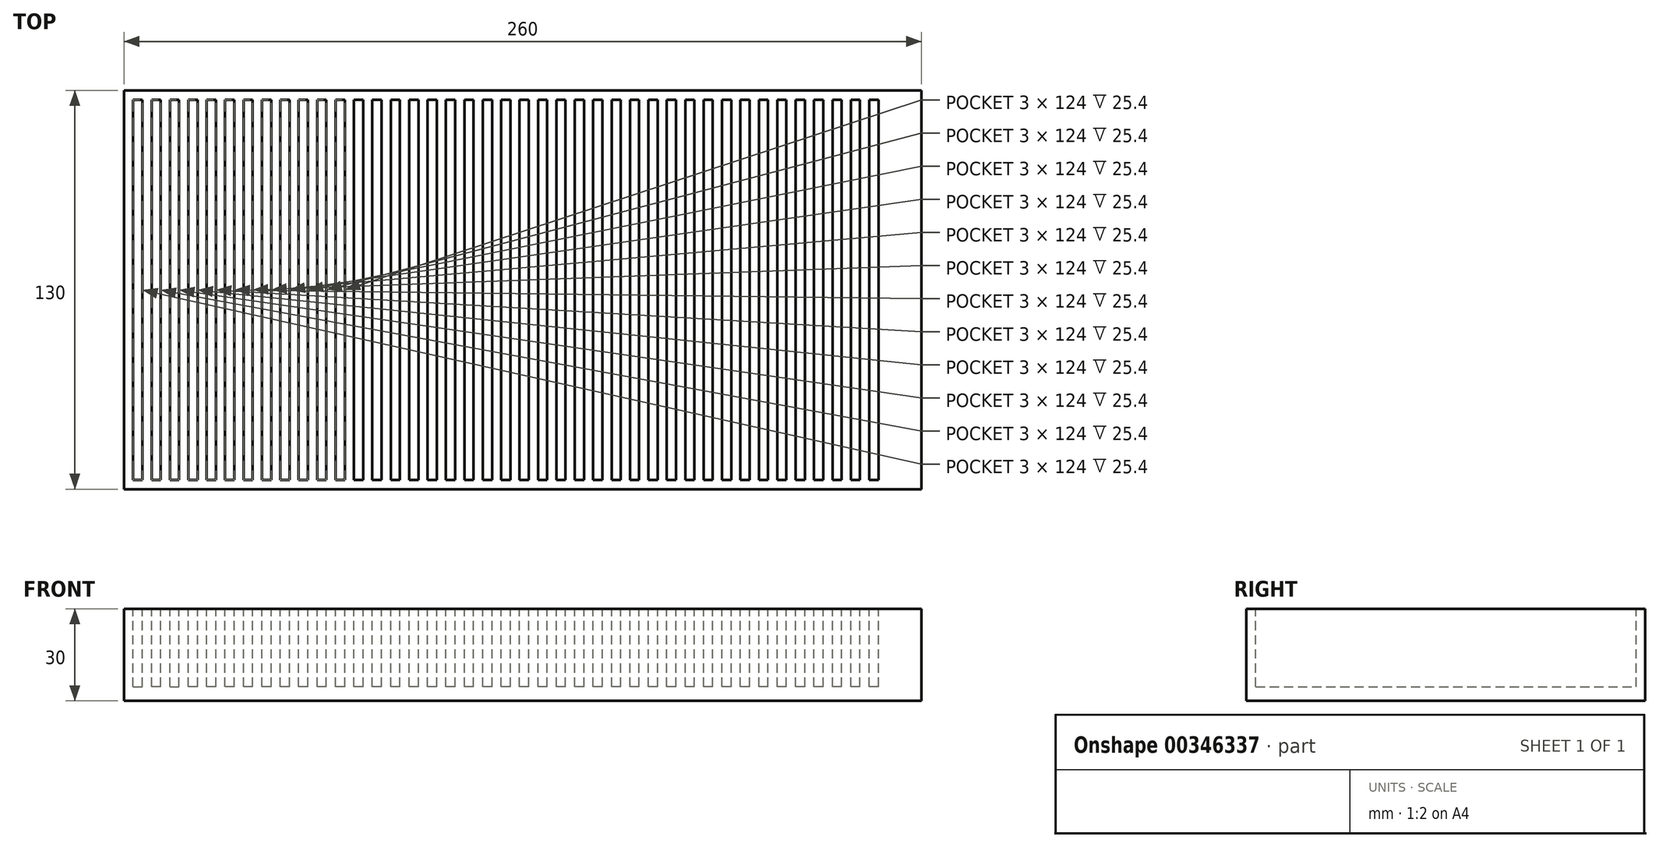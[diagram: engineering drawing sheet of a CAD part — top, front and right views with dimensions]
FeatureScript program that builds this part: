
annotation { "Feature Type Name" : "Feature", "Feature Type Description" : "" }
export const myFeature = defineFeature(function(context is Context, id is Id, definition is map)
    precondition{}
    {
        {
            var Q0;
            Q0=qCreatedBy(makeId("Top.planeOp"),FACE);
            var sketch = newSketch(context, id + "F0", { "sketchPlane" : qUnion([Q0])});
            skLineSegment(sketch, "E0.bottom", {"start": v(-130, 65) * mm, "end": v(130, 65) * mm});
            skLineSegment(sketch, "E0.top", {"start": v(-130, -65) * mm, "end": v(130, -65) * mm});
            skLineSegment(sketch, "E0.left", {"start": v(-130, 65) * mm, "end": v(-130, -65) * mm});
            skLineSegment(sketch, "E0.right", {"start": v(130, 65) * mm, "end": v(130, -65) * mm});
            skPoint(sketch, "E0.middle", {"position": v(0, 0) * mm});
            skSolve(sketch);
        }
        {
            var Q0;
            Q0=makeQuery(id+"F0.imprint","IMPRINT",FACE,{"disambiguationData":[TD([[makeQuery(id+"F0.imprint","IMPRINT",EDGE,{"derivedFrom":sQuery(id+"F0.wireOp",EDGE,"E0.bottom")}),-1.0]])]});
            extrude(context, id + "F1", {"entities" : qUnion([Q0]), "depth" : 30 * mm});
        }
        {
            var Q0;
            Q0=makeQuery(id+"F1.opExtrude","CAP_FACE",FACE,{"disambiguationData":[OSD([sQuery(id+"F0.wireOp",EDGE,"E0.bottom"),sQuery(id+"F0.wireOp",EDGE,"E0.top"),sQuery(id+"F0.wireOp",EDGE,"E0.left"),sQuery(id+"F0.wireOp",EDGE,"E0.right")])],"isStart":false});
            var sketch = newSketch(context, id + "F2", { "sketchPlane" : qUnion([Q0])});
            skLineSegment(sketch, "E1.0", {"start": v(-127, 62) * mm, "end": v(-127, -62) * mm});
            skLineSegment(sketch, "E1.1", {"start": v(127, 62) * mm, "end": v(-127, 62) * mm});
            skLineSegment(sketch, "E1.2", {"start": v(127, -62) * mm, "end": v(127, 62) * mm});
            skLineSegment(sketch, "E1.3", {"start": v(-127, -62) * mm, "end": v(127, -62) * mm});
            skLineSegment(sketch, "E2", {"start": v(-127, 0) * mm, "end": v(-124, 0) * mm});
            skLineSegment(sketch, "E3", {"start": v(-124, 0) * mm, "end": v(-121, 0) * mm});
            skLineSegment(sketch, "E4", {"start": v(-121, 0) * mm, "end": v(-118, 0) * mm});
            skLineSegment(sketch, "E5", {"start": v(-118, 0) * mm, "end": v(-115, 0) * mm});
            skLineSegment(sketch, "E6", {"start": v(-115, 0) * mm, "end": v(-112, 0) * mm});
            skLineSegment(sketch, "E7", {"start": v(-112, 0) * mm, "end": v(-109, 0) * mm});
            skLineSegment(sketch, "E8", {"start": v(-109, 0) * mm, "end": v(-106, 0) * mm});
            skLineSegment(sketch, "E9", {"start": v(-106, 0) * mm, "end": v(-103, 0) * mm});
            skLineSegment(sketch, "E10", {"start": v(-103, 0) * mm, "end": v(-100, 0) * mm});
            skLineSegment(sketch, "E11", {"start": v(-100, 0) * mm, "end": v(-97, 0) * mm});
            skLineSegment(sketch, "E12", {"start": v(-97, 0) * mm, "end": v(-94, 0) * mm});
            skLineSegment(sketch, "E13", {"start": v(-94, 0) * mm, "end": v(-91, 0) * mm});
            skLineSegment(sketch, "E14", {"start": v(-91, 0) * mm, "end": v(-88, 0) * mm});
            skLineSegment(sketch, "E15", {"start": v(-88, 0) * mm, "end": v(-85, 0) * mm});
            skLineSegment(sketch, "E16", {"start": v(-85, 0) * mm, "end": v(-82, 0) * mm});
            skLineSegment(sketch, "E17", {"start": v(-82, 0) * mm, "end": v(-79, 0) * mm});
            skLineSegment(sketch, "E18", {"start": v(-79, 0) * mm, "end": v(-76, 0) * mm});
            skLineSegment(sketch, "E19", {"start": v(-124, 0) * mm, "end": v(-124, 62) * mm});
            skLineSegment(sketch, "E20", {"start": v(-121, 0) * mm, "end": v(-121, 4.03) * mm});
            skLineSegment(sketch, "E21", {"start": v(-121, 62) * mm, "end": v(-121, 0) * mm});
            skLineSegment(sketch, "E22", {"start": v(-118, 0) * mm, "end": v(-118, 62) * mm});
            skLineSegment(sketch, "E23", {"start": v(-118, 62) * mm, "end": v(-115, 62) * mm});
            skLineSegment(sketch, "E24", {"start": v(-115, 62) * mm, "end": v(-115, 0) * mm});
            skLineSegment(sketch, "E25", {"start": v(-112, 0) * mm, "end": v(-112, 62) * mm});
            skLineSegment(sketch, "E26", {"start": v(-112, 62) * mm, "end": v(-109, 62) * mm});
            skLineSegment(sketch, "E27", {"start": v(-109, 62) * mm, "end": v(-109, 0) * mm});
            skLineSegment(sketch, "E28", {"start": v(-106, 0) * mm, "end": v(-106, 62) * mm});
            skLineSegment(sketch, "E29", {"start": v(-106, 62) * mm, "end": v(-103, 62) * mm});
            skLineSegment(sketch, "E30", {"start": v(-103, 62) * mm, "end": v(-103, -62) * mm});
            skLineSegment(sketch, "E31", {"start": v(-103, -62) * mm, "end": v(-100, -62) * mm});
            skLineSegment(sketch, "E32", {"start": v(-100, -62) * mm, "end": v(-100, 62) * mm});
            skLineSegment(sketch, "E33", {"start": v(-100, 62) * mm, "end": v(-97, 62) * mm});
            skLineSegment(sketch, "E34", {"start": v(-97, 62) * mm, "end": v(-97, -62) * mm});
            skLineSegment(sketch, "E35", {"start": v(-97, -62) * mm, "end": v(-94, -62) * mm});
            skLineSegment(sketch, "E36", {"start": v(-94, -62) * mm, "end": v(-94, 62) * mm});
            skLineSegment(sketch, "E37", {"start": v(-94, 62) * mm, "end": v(-91, 62) * mm});
            skLineSegment(sketch, "E38", {"start": v(-91, 62) * mm, "end": v(-91, -62) * mm});
            skLineSegment(sketch, "E39", {"start": v(-91, -62) * mm, "end": v(-88, -62) * mm});
            skLineSegment(sketch, "E40", {"start": v(-88, -62) * mm, "end": v(-88, 62) * mm});
            skLineSegment(sketch, "E41", {"start": v(-88, 62) * mm, "end": v(-85, 62) * mm});
            skLineSegment(sketch, "E42", {"start": v(-85, 62) * mm, "end": v(-85, -62) * mm});
            skLineSegment(sketch, "E43", {"start": v(-85, -62) * mm, "end": v(-82, -62) * mm});
            skLineSegment(sketch, "E44", {"start": v(-82, -62) * mm, "end": v(-82, 62) * mm});
            skLineSegment(sketch, "E45", {"start": v(-82, 62) * mm, "end": v(-79, 62) * mm});
            skLineSegment(sketch, "E46", {"start": v(-79, 62) * mm, "end": v(-79, -62) * mm});
            skLineSegment(sketch, "E47", {"start": v(-79, -62) * mm, "end": v(-76, -62) * mm});
            skLineSegment(sketch, "E48", {"start": v(-76, -62) * mm, "end": v(-76, 62) * mm});
            skLineSegment(sketch, "E49", {"start": v(-106, 0) * mm, "end": v(-106, -62) * mm});
            skLineSegment(sketch, "E50", {"start": v(-106, -62) * mm, "end": v(-109, -62) * mm});
            skLineSegment(sketch, "E51", {"start": v(-109, -62) * mm, "end": v(-109, 0) * mm});
            skLineSegment(sketch, "E52", {"start": v(-112, 0) * mm, "end": v(-112, -62) * mm});
            skLineSegment(sketch, "E53", {"start": v(-112, -62) * mm, "end": v(-115, -62) * mm});
            skLineSegment(sketch, "E54", {"start": v(-115, -62) * mm, "end": v(-115, 0) * mm});
            skLineSegment(sketch, "E55", {"start": v(-118, 0) * mm, "end": v(-118, -62) * mm});
            skLineSegment(sketch, "E56", {"start": v(-118, -62) * mm, "end": v(-121, -62) * mm});
            skLineSegment(sketch, "E57", {"start": v(-121, -62) * mm, "end": v(-121, 0) * mm});
            skLineSegment(sketch, "E58", {"start": v(-124, 0) * mm, "end": v(-124, -62) * mm});
            skLineSegment(sketch, "E59", {"start": v(-76, 62) * mm, "end": v(-73, 62) * mm});
            skLineSegment(sketch, "E60", {"start": v(-73, 62) * mm, "end": v(-73, -62) * mm});
            skLineSegment(sketch, "E61", {"start": v(-73, -62) * mm, "end": v(-70, -62) * mm});
            skLineSegment(sketch, "E62", {"start": v(-70, -62) * mm, "end": v(-70, 62) * mm});
            skLineSegment(sketch, "E63", {"start": v(-70, 62) * mm, "end": v(-67, 62) * mm});
            skLineSegment(sketch, "E64", {"start": v(-67, 62) * mm, "end": v(-67, -62) * mm});
            skLineSegment(sketch, "E65", {"start": v(-67, -62) * mm, "end": v(-64, -62) * mm});
            skLineSegment(sketch, "E66", {"start": v(-64, -62) * mm, "end": v(-64, 62) * mm});
            skLineSegment(sketch, "E67", {"start": v(-64, 62) * mm, "end": v(-61, 62) * mm});
            skLineSegment(sketch, "E68", {"start": v(-61, 62) * mm, "end": v(-61, -62) * mm});
            skLineSegment(sketch, "E69", {"start": v(-61, -62) * mm, "end": v(-58, -62) * mm});
            skLineSegment(sketch, "E70", {"start": v(-58, -62) * mm, "end": v(-58, 62) * mm});
            skLineSegment(sketch, "E71", {"start": v(-58, 62) * mm, "end": v(-55, 62) * mm});
            skLineSegment(sketch, "E72", {"start": v(-55, 62) * mm, "end": v(-55, -62) * mm});
            skLineSegment(sketch, "E73", {"start": v(-55, -62) * mm, "end": v(-52, -62) * mm});
            skLineSegment(sketch, "E74", {"start": v(-52, -62) * mm, "end": v(-52, 62) * mm});
            skLineSegment(sketch, "E75", {"start": v(-52, 62) * mm, "end": v(-49, 62) * mm});
            skLineSegment(sketch, "E76", {"start": v(-49, 62) * mm, "end": v(-49, -62) * mm});
            skLineSegment(sketch, "E77", {"start": v(-49, -62) * mm, "end": v(-46, -62) * mm});
            skLineSegment(sketch, "E78", {"start": v(-46, -62) * mm, "end": v(-46, 62) * mm});
            skLineSegment(sketch, "E79", {"start": v(-46, 62) * mm, "end": v(-43, 62) * mm});
            skLineSegment(sketch, "E80", {"start": v(-43, 62) * mm, "end": v(-43, -62) * mm});
            skLineSegment(sketch, "E81", {"start": v(-43, -62) * mm, "end": v(-40, -62) * mm});
            skLineSegment(sketch, "E82", {"start": v(-40, -62) * mm, "end": v(-40, 62) * mm});
            skLineSegment(sketch, "E83", {"start": v(-40, 62) * mm, "end": v(-37, 62) * mm});
            skLineSegment(sketch, "E84", {"start": v(-37, 62) * mm, "end": v(-37, -62) * mm});
            skLineSegment(sketch, "E85", {"start": v(-37, -62) * mm, "end": v(-34, -62) * mm});
            skLineSegment(sketch, "E86", {"start": v(-34, -62) * mm, "end": v(-34, 62) * mm});
            skLineSegment(sketch, "E87", {"start": v(-34, 62) * mm, "end": v(-31, 62) * mm});
            skLineSegment(sketch, "E88", {"start": v(-31, 62) * mm, "end": v(-31, -62) * mm});
            skLineSegment(sketch, "E89", {"start": v(-31, -62) * mm, "end": v(-28, -62) * mm});
            skLineSegment(sketch, "E90", {"start": v(-28, -62) * mm, "end": v(-28, 62) * mm});
            skLineSegment(sketch, "E91", {"start": v(-28, 62) * mm, "end": v(-25, 62) * mm});
            skLineSegment(sketch, "E92", {"start": v(-25, 62) * mm, "end": v(-25, -62) * mm});
            skLineSegment(sketch, "E93", {"start": v(-25, -62) * mm, "end": v(-22, -62) * mm});
            skLineSegment(sketch, "E94", {"start": v(-22, -62) * mm, "end": v(-22, 62) * mm});
            skLineSegment(sketch, "E95", {"start": v(-22, 62) * mm, "end": v(-19, 62) * mm});
            skLineSegment(sketch, "E96", {"start": v(-19, 62) * mm, "end": v(-19, -62) * mm});
            skLineSegment(sketch, "E97", {"start": v(-19, -62) * mm, "end": v(-16, -62) * mm});
            skLineSegment(sketch, "E98", {"start": v(-16, -62) * mm, "end": v(-16, 62) * mm});
            skLineSegment(sketch, "E99", {"start": v(-16, 62) * mm, "end": v(-13, 62) * mm});
            skLineSegment(sketch, "E100", {"start": v(-13, 62) * mm, "end": v(-13, -62) * mm});
            skLineSegment(sketch, "E101", {"start": v(-13, -62) * mm, "end": v(-10, -62) * mm});
            skLineSegment(sketch, "E102", {"start": v(-10, -62) * mm, "end": v(-10, 62) * mm});
            skLineSegment(sketch, "E103", {"start": v(-10, 62) * mm, "end": v(-7, 62) * mm});
            skLineSegment(sketch, "E104", {"start": v(-7, 62) * mm, "end": v(-7, -62) * mm});
            skLineSegment(sketch, "E105", {"start": v(-7, -62) * mm, "end": v(-4, -62) * mm});
            skLineSegment(sketch, "E106", {"start": v(-4, -62) * mm, "end": v(-4, 62) * mm});
            skLineSegment(sketch, "E107", {"start": v(-4, 62) * mm, "end": v(-1, 62) * mm});
            skLineSegment(sketch, "E108", {"start": v(-1, 62) * mm, "end": v(-1, -62) * mm});
            skLineSegment(sketch, "E109", {"start": v(-1, -62) * mm, "end": v(2, -62) * mm});
            skLineSegment(sketch, "E110", {"start": v(2, -62) * mm, "end": v(2, 62) * mm});
            skLineSegment(sketch, "E111", {"start": v(2, 62) * mm, "end": v(5, 62) * mm});
            skLineSegment(sketch, "E112", {"start": v(5, 62) * mm, "end": v(5, -62) * mm});
            skLineSegment(sketch, "E113", {"start": v(5, -62) * mm, "end": v(8, -62) * mm});
            skLineSegment(sketch, "E114", {"start": v(8, -62) * mm, "end": v(8, 62) * mm});
            skLineSegment(sketch, "E115", {"start": v(8, 62) * mm, "end": v(11, 62) * mm});
            skLineSegment(sketch, "E116", {"start": v(11, 62) * mm, "end": v(11, -62) * mm});
            skLineSegment(sketch, "E117", {"start": v(11, -62) * mm, "end": v(14, -62) * mm});
            skLineSegment(sketch, "E118", {"start": v(14, -62) * mm, "end": v(14, 62) * mm});
            skLineSegment(sketch, "E119", {"start": v(14, 62) * mm, "end": v(17, 62) * mm});
            skLineSegment(sketch, "E120", {"start": v(17, 62) * mm, "end": v(17, -62) * mm});
            skLineSegment(sketch, "E121", {"start": v(17, -62) * mm, "end": v(20, -62) * mm});
            skLineSegment(sketch, "E122", {"start": v(20, -62) * mm, "end": v(20, 62) * mm});
            skLineSegment(sketch, "E123", {"start": v(20, 62) * mm, "end": v(23, 62) * mm});
            skLineSegment(sketch, "E124", {"start": v(23, 62) * mm, "end": v(23, -62) * mm});
            skLineSegment(sketch, "E125", {"start": v(23, -62) * mm, "end": v(26, -62) * mm});
            skLineSegment(sketch, "E126", {"start": v(26, -62) * mm, "end": v(26, 62) * mm});
            skLineSegment(sketch, "E127", {"start": v(26, 62) * mm, "end": v(29, 62) * mm});
            skLineSegment(sketch, "E128", {"start": v(29, 62) * mm, "end": v(29, -62) * mm});
            skLineSegment(sketch, "E129", {"start": v(29, -62) * mm, "end": v(32, -62) * mm});
            skLineSegment(sketch, "E130", {"start": v(32, -62) * mm, "end": v(32, 62) * mm});
            skLineSegment(sketch, "E131", {"start": v(32, 62) * mm, "end": v(35, 62) * mm});
            skLineSegment(sketch, "E132", {"start": v(35, 62) * mm, "end": v(35, -62) * mm});
            skLineSegment(sketch, "E133", {"start": v(35, -62) * mm, "end": v(38, -62) * mm});
            skLineSegment(sketch, "E134", {"start": v(38, -62) * mm, "end": v(38, 62) * mm});
            skLineSegment(sketch, "E135", {"start": v(38, 62) * mm, "end": v(41, 62) * mm});
            skLineSegment(sketch, "E136", {"start": v(41, 62) * mm, "end": v(41, -62) * mm});
            skLineSegment(sketch, "E137", {"start": v(41, -62) * mm, "end": v(44, -62) * mm});
            skLineSegment(sketch, "E138", {"start": v(44, -62) * mm, "end": v(44, 62) * mm});
            skLineSegment(sketch, "E139", {"start": v(44, 62) * mm, "end": v(47, 62) * mm});
            skLineSegment(sketch, "E140", {"start": v(47, 62) * mm, "end": v(47, -62) * mm});
            skLineSegment(sketch, "E141", {"start": v(47, -62) * mm, "end": v(50, -62) * mm});
            skLineSegment(sketch, "E142", {"start": v(50, -62) * mm, "end": v(50, 62) * mm});
            skLineSegment(sketch, "E143", {"start": v(50, 62) * mm, "end": v(53, 62) * mm});
            skLineSegment(sketch, "E144", {"start": v(53, 62) * mm, "end": v(53, -62) * mm});
            skLineSegment(sketch, "E145", {"start": v(53, -62) * mm, "end": v(56, -62) * mm});
            skLineSegment(sketch, "E146", {"start": v(56, -62) * mm, "end": v(56, 62) * mm});
            skLineSegment(sketch, "E147", {"start": v(56, 62) * mm, "end": v(59, 62) * mm});
            skLineSegment(sketch, "E148", {"start": v(59, 62) * mm, "end": v(59, -62) * mm});
            skLineSegment(sketch, "E149", {"start": v(59, -62) * mm, "end": v(62, -62) * mm});
            skLineSegment(sketch, "E150", {"start": v(62, -62) * mm, "end": v(62, 62) * mm});
            skLineSegment(sketch, "E151", {"start": v(62, 62) * mm, "end": v(65, 62) * mm});
            skLineSegment(sketch, "E152", {"start": v(65, 62) * mm, "end": v(65, -62) * mm});
            skLineSegment(sketch, "E153", {"start": v(65, -62) * mm, "end": v(68, -62) * mm});
            skLineSegment(sketch, "E154", {"start": v(68, -62) * mm, "end": v(68, 62) * mm});
            skLineSegment(sketch, "E155", {"start": v(68, 62) * mm, "end": v(71, 62) * mm});
            skLineSegment(sketch, "E156", {"start": v(71, 62) * mm, "end": v(71, -62) * mm});
            skLineSegment(sketch, "E157", {"start": v(71, -62) * mm, "end": v(74, -62) * mm});
            skLineSegment(sketch, "E158", {"start": v(74, -62) * mm, "end": v(74, 62) * mm});
            skLineSegment(sketch, "E159", {"start": v(74, 62) * mm, "end": v(77, 62) * mm});
            skLineSegment(sketch, "E160", {"start": v(77, 62) * mm, "end": v(77, -62) * mm});
            skLineSegment(sketch, "E161", {"start": v(77, -62) * mm, "end": v(80, -62) * mm});
            skLineSegment(sketch, "E162", {"start": v(80, -62) * mm, "end": v(80, 62) * mm});
            skLineSegment(sketch, "E163", {"start": v(80, 62) * mm, "end": v(83, 62) * mm});
            skLineSegment(sketch, "E164", {"start": v(83, 62) * mm, "end": v(83, -62) * mm});
            skLineSegment(sketch, "E165", {"start": v(83, -62) * mm, "end": v(86, -62) * mm});
            skLineSegment(sketch, "E166", {"start": v(86, -62) * mm, "end": v(86, 62) * mm});
            skLineSegment(sketch, "E167", {"start": v(86, 62) * mm, "end": v(89, 62) * mm});
            skLineSegment(sketch, "E168", {"start": v(89, 62) * mm, "end": v(89, -62) * mm});
            skLineSegment(sketch, "E169", {"start": v(89, -62) * mm, "end": v(92, -62) * mm});
            skLineSegment(sketch, "E170", {"start": v(92, -62) * mm, "end": v(92, 62) * mm});
            skLineSegment(sketch, "E171", {"start": v(92, 62) * mm, "end": v(95, 62) * mm});
            skLineSegment(sketch, "E172", {"start": v(95, 62) * mm, "end": v(95, -62) * mm});
            skLineSegment(sketch, "E173", {"start": v(95, -62) * mm, "end": v(98, -62) * mm});
            skLineSegment(sketch, "E174", {"start": v(98, -62) * mm, "end": v(98, 62) * mm});
            skLineSegment(sketch, "E175", {"start": v(98, 62) * mm, "end": v(101, 62) * mm});
            skLineSegment(sketch, "E176", {"start": v(101, 62) * mm, "end": v(101, -62) * mm});
            skLineSegment(sketch, "E177", {"start": v(101, -62) * mm, "end": v(104, -62) * mm});
            skLineSegment(sketch, "E178", {"start": v(104, -62) * mm, "end": v(104, 62) * mm});
            skLineSegment(sketch, "E179", {"start": v(104, 62) * mm, "end": v(107, 62) * mm});
            skLineSegment(sketch, "E180", {"start": v(107, 62) * mm, "end": v(107, -62) * mm});
            skLineSegment(sketch, "E181", {"start": v(107, -62) * mm, "end": v(110, -62) * mm});
            skLineSegment(sketch, "E182", {"start": v(110, -62) * mm, "end": v(110, 62) * mm});
            skLineSegment(sketch, "E183", {"start": v(110, 62) * mm, "end": v(113, 62) * mm});
            skLineSegment(sketch, "E184", {"start": v(113, 62) * mm, "end": v(113, -62) * mm});
            skLineSegment(sketch, "E185", {"start": v(113, -62) * mm, "end": v(116, -62) * mm});
            skLineSegment(sketch, "E186", {"start": v(116, -62) * mm, "end": v(116, 62) * mm});
            skSolve(sketch);
        }
        {
            var Q0;
            {var subQ3=sQuery(id+"F2.wireOp",EDGE,"E2");Q0=makeQuery(id+"F2.imprint","IMPRINT",FACE,{"disambiguationData":[TD([[makeQuery(id+"F2.imprint","IMPRINT",EDGE,{"derivedFrom":subQ3}),1.0]])]});}
            var Q1;
            {var subQ3=sQuery(id+"F2.wireOp",EDGE,"E2");Q1=makeQuery(id+"F2.imprint","IMPRINT",FACE,{"disambiguationData":[TD([[makeQuery(id+"F2.imprint","IMPRINT",EDGE,{"derivedFrom":subQ3}),-1.0]])]});}
            var Q2;
            {var subQ1=sQuery(id+"F2.wireOp",EDGE,"E4");Q2=makeQuery(id+"F2.imprint","IMPRINT",FACE,{"disambiguationData":[TD([[makeQuery(id+"F2.imprint","IMPRINT",EDGE,{"derivedFrom":subQ1}),1.0]])]});}
            var Q3;
            Q3=makeQuery(id+"F2.imprint","IMPRINT",FACE,{"disambiguationData":[TD([[makeQuery(id+"F2.imprint","IMPRINT",EDGE,{"derivedFrom":sQuery(id+"F2.wireOp",EDGE,"E4")}),-1.0]])]});
            var Q4;
            Q4=makeQuery(id+"F2.imprint","IMPRINT",FACE,{"disambiguationData":[TD([[makeQuery(id+"F2.imprint","IMPRINT",EDGE,{"derivedFrom":sQuery(id+"F2.wireOp",EDGE,"E6")}),1.0]])]});
            var Q5;
            Q5=makeQuery(id+"F2.imprint","IMPRINT",FACE,{"disambiguationData":[TD([[makeQuery(id+"F2.imprint","IMPRINT",EDGE,{"derivedFrom":sQuery(id+"F2.wireOp",EDGE,"E6")}),-1.0]])]});
            var Q6;
            Q6=makeQuery(id+"F2.imprint","IMPRINT",FACE,{"disambiguationData":[TD([[makeQuery(id+"F2.imprint","IMPRINT",EDGE,{"derivedFrom":sQuery(id+"F2.wireOp",EDGE,"E8")}),1.0]])]});
            var Q7;
            Q7=makeQuery(id+"F2.imprint","IMPRINT",FACE,{"disambiguationData":[TD([[makeQuery(id+"F2.imprint","IMPRINT",EDGE,{"derivedFrom":sQuery(id+"F2.wireOp",EDGE,"E8")}),-1.0]])]});
            var Q8;
            {var subQ5=sQuery(id+"F2.wireOp",EDGE,"E10");Q8=makeQuery(id+"F2.imprint","IMPRINT",FACE,{"disambiguationData":[TD([[makeQuery(id+"F2.imprint","IMPRINT",EDGE,{"derivedFrom":subQ5}),1.0]])]});}
            var Q9;
            {var subQ0=sQuery(id+"F2.wireOp",EDGE,"E10");Q9=makeQuery(id+"F2.imprint","IMPRINT",FACE,{"disambiguationData":[TD([[makeQuery(id+"F2.imprint","IMPRINT",EDGE,{"derivedFrom":subQ0}),-1.0]])]});}
            var Q10;
            {var subQ5=sQuery(id+"F2.wireOp",EDGE,"E12");Q10=makeQuery(id+"F2.imprint","IMPRINT",FACE,{"disambiguationData":[TD([[makeQuery(id+"F2.imprint","IMPRINT",EDGE,{"derivedFrom":subQ5}),1.0]])]});}
            var Q11;
            {var subQ0=sQuery(id+"F2.wireOp",EDGE,"E12");Q11=makeQuery(id+"F2.imprint","IMPRINT",FACE,{"disambiguationData":[TD([[makeQuery(id+"F2.imprint","IMPRINT",EDGE,{"derivedFrom":subQ0}),-1.0]])]});}
            var Q12;
            {var subQ5=sQuery(id+"F2.wireOp",EDGE,"E14");Q12=makeQuery(id+"F2.imprint","IMPRINT",FACE,{"disambiguationData":[TD([[makeQuery(id+"F2.imprint","IMPRINT",EDGE,{"derivedFrom":subQ5}),1.0]])]});}
            var Q13;
            {var subQ0=sQuery(id+"F2.wireOp",EDGE,"E14");Q13=makeQuery(id+"F2.imprint","IMPRINT",FACE,{"disambiguationData":[TD([[makeQuery(id+"F2.imprint","IMPRINT",EDGE,{"derivedFrom":subQ0}),-1.0]])]});}
            var Q14;
            {var subQ5=sQuery(id+"F2.wireOp",EDGE,"E16");Q14=makeQuery(id+"F2.imprint","IMPRINT",FACE,{"disambiguationData":[TD([[makeQuery(id+"F2.imprint","IMPRINT",EDGE,{"derivedFrom":subQ5}),1.0]])]});}
            var Q15;
            {var subQ0=sQuery(id+"F2.wireOp",EDGE,"E16");Q15=makeQuery(id+"F2.imprint","IMPRINT",FACE,{"disambiguationData":[TD([[makeQuery(id+"F2.imprint","IMPRINT",EDGE,{"derivedFrom":subQ0}),-1.0]])]});}
            var Q16;
            {var subQ5=sQuery(id+"F2.wireOp",EDGE,"E18");Q16=makeQuery(id+"F2.imprint","IMPRINT",FACE,{"disambiguationData":[TD([[makeQuery(id+"F2.imprint","IMPRINT",EDGE,{"derivedFrom":subQ5}),1.0]])]});}
            var Q17;
            {var subQ0=sQuery(id+"F2.wireOp",EDGE,"E18");Q17=makeQuery(id+"F2.imprint","IMPRINT",FACE,{"disambiguationData":[TD([[makeQuery(id+"F2.imprint","IMPRINT",EDGE,{"derivedFrom":subQ0}),-1.0]])]});}
            var Q18;
            {var subQ0=sQuery(id+"F2.wireOp",EDGE,"E60");Q18=makeQuery(id+"F2.imprint","IMPRINT",FACE,{"disambiguationData":[TD([[makeQuery(id+"F2.imprint","IMPRINT",EDGE,{"derivedFrom":subQ0}),1.0]])]});}
            var Q19;
            {var subQ0=sQuery(id+"F2.wireOp",EDGE,"E64");Q19=makeQuery(id+"F2.imprint","IMPRINT",FACE,{"disambiguationData":[TD([[makeQuery(id+"F2.imprint","IMPRINT",EDGE,{"derivedFrom":subQ0}),1.0]])]});}
            var Q20;
            {var subQ0=sQuery(id+"F2.wireOp",EDGE,"E68");Q20=makeQuery(id+"F2.imprint","IMPRINT",FACE,{"disambiguationData":[TD([[makeQuery(id+"F2.imprint","IMPRINT",EDGE,{"derivedFrom":subQ0}),1.0]])]});}
            var Q21;
            {var subQ0=sQuery(id+"F2.wireOp",EDGE,"E72");Q21=makeQuery(id+"F2.imprint","IMPRINT",FACE,{"disambiguationData":[TD([[makeQuery(id+"F2.imprint","IMPRINT",EDGE,{"derivedFrom":subQ0}),1.0]])]});}
            var Q22;
            {var subQ0=sQuery(id+"F2.wireOp",EDGE,"E76");Q22=makeQuery(id+"F2.imprint","IMPRINT",FACE,{"disambiguationData":[TD([[makeQuery(id+"F2.imprint","IMPRINT",EDGE,{"derivedFrom":subQ0}),1.0]])]});}
            var Q23;
            {var subQ0=sQuery(id+"F2.wireOp",EDGE,"E80");Q23=makeQuery(id+"F2.imprint","IMPRINT",FACE,{"disambiguationData":[TD([[makeQuery(id+"F2.imprint","IMPRINT",EDGE,{"derivedFrom":subQ0}),1.0]])]});}
            var Q24;
            {var subQ0=sQuery(id+"F2.wireOp",EDGE,"E84");Q24=makeQuery(id+"F2.imprint","IMPRINT",FACE,{"disambiguationData":[TD([[makeQuery(id+"F2.imprint","IMPRINT",EDGE,{"derivedFrom":subQ0}),1.0]])]});}
            var Q25;
            {var subQ0=sQuery(id+"F2.wireOp",EDGE,"E88");Q25=makeQuery(id+"F2.imprint","IMPRINT",FACE,{"disambiguationData":[TD([[makeQuery(id+"F2.imprint","IMPRINT",EDGE,{"derivedFrom":subQ0}),1.0]])]});}
            var Q26;
            {var subQ0=sQuery(id+"F2.wireOp",EDGE,"E92");Q26=makeQuery(id+"F2.imprint","IMPRINT",FACE,{"disambiguationData":[TD([[makeQuery(id+"F2.imprint","IMPRINT",EDGE,{"derivedFrom":subQ0}),1.0]])]});}
            var Q27;
            {var subQ0=sQuery(id+"F2.wireOp",EDGE,"E96");Q27=makeQuery(id+"F2.imprint","IMPRINT",FACE,{"disambiguationData":[TD([[makeQuery(id+"F2.imprint","IMPRINT",EDGE,{"derivedFrom":subQ0}),1.0]])]});}
            var Q28;
            {var subQ0=sQuery(id+"F2.wireOp",EDGE,"E100");Q28=makeQuery(id+"F2.imprint","IMPRINT",FACE,{"disambiguationData":[TD([[makeQuery(id+"F2.imprint","IMPRINT",EDGE,{"derivedFrom":subQ0}),1.0]])]});}
            var Q29;
            {var subQ0=sQuery(id+"F2.wireOp",EDGE,"E104");Q29=makeQuery(id+"F2.imprint","IMPRINT",FACE,{"disambiguationData":[TD([[makeQuery(id+"F2.imprint","IMPRINT",EDGE,{"derivedFrom":subQ0}),1.0]])]});}
            var Q30;
            {var subQ0=sQuery(id+"F2.wireOp",EDGE,"E108");Q30=makeQuery(id+"F2.imprint","IMPRINT",FACE,{"disambiguationData":[TD([[makeQuery(id+"F2.imprint","IMPRINT",EDGE,{"derivedFrom":subQ0}),1.0]])]});}
            var Q31;
            {var subQ0=sQuery(id+"F2.wireOp",EDGE,"E112");Q31=makeQuery(id+"F2.imprint","IMPRINT",FACE,{"disambiguationData":[TD([[makeQuery(id+"F2.imprint","IMPRINT",EDGE,{"derivedFrom":subQ0}),1.0]])]});}
            var Q32;
            {var subQ0=sQuery(id+"F2.wireOp",EDGE,"E116");Q32=makeQuery(id+"F2.imprint","IMPRINT",FACE,{"disambiguationData":[TD([[makeQuery(id+"F2.imprint","IMPRINT",EDGE,{"derivedFrom":subQ0}),1.0]])]});}
            var Q33;
            {var subQ0=sQuery(id+"F2.wireOp",EDGE,"E120");Q33=makeQuery(id+"F2.imprint","IMPRINT",FACE,{"disambiguationData":[TD([[makeQuery(id+"F2.imprint","IMPRINT",EDGE,{"derivedFrom":subQ0}),1.0]])]});}
            var Q34;
            {var subQ0=sQuery(id+"F2.wireOp",EDGE,"E124");Q34=makeQuery(id+"F2.imprint","IMPRINT",FACE,{"disambiguationData":[TD([[makeQuery(id+"F2.imprint","IMPRINT",EDGE,{"derivedFrom":subQ0}),1.0]])]});}
            var Q35;
            {var subQ0=sQuery(id+"F2.wireOp",EDGE,"E128");Q35=makeQuery(id+"F2.imprint","IMPRINT",FACE,{"disambiguationData":[TD([[makeQuery(id+"F2.imprint","IMPRINT",EDGE,{"derivedFrom":subQ0}),1.0]])]});}
            var Q36;
            {var subQ0=sQuery(id+"F2.wireOp",EDGE,"E132");Q36=makeQuery(id+"F2.imprint","IMPRINT",FACE,{"disambiguationData":[TD([[makeQuery(id+"F2.imprint","IMPRINT",EDGE,{"derivedFrom":subQ0}),1.0]])]});}
            var Q37;
            {var subQ0=sQuery(id+"F2.wireOp",EDGE,"E136");Q37=makeQuery(id+"F2.imprint","IMPRINT",FACE,{"disambiguationData":[TD([[makeQuery(id+"F2.imprint","IMPRINT",EDGE,{"derivedFrom":subQ0}),1.0]])]});}
            var Q38;
            {var subQ0=sQuery(id+"F2.wireOp",EDGE,"E140");Q38=makeQuery(id+"F2.imprint","IMPRINT",FACE,{"disambiguationData":[TD([[makeQuery(id+"F2.imprint","IMPRINT",EDGE,{"derivedFrom":subQ0}),1.0]])]});}
            var Q39;
            {var subQ0=sQuery(id+"F2.wireOp",EDGE,"E144");Q39=makeQuery(id+"F2.imprint","IMPRINT",FACE,{"disambiguationData":[TD([[makeQuery(id+"F2.imprint","IMPRINT",EDGE,{"derivedFrom":subQ0}),1.0]])]});}
            var Q40;
            {var subQ0=sQuery(id+"F2.wireOp",EDGE,"E148");Q40=makeQuery(id+"F2.imprint","IMPRINT",FACE,{"disambiguationData":[TD([[makeQuery(id+"F2.imprint","IMPRINT",EDGE,{"derivedFrom":subQ0}),1.0]])]});}
            var Q41;
            {var subQ0=sQuery(id+"F2.wireOp",EDGE,"E152");Q41=makeQuery(id+"F2.imprint","IMPRINT",FACE,{"disambiguationData":[TD([[makeQuery(id+"F2.imprint","IMPRINT",EDGE,{"derivedFrom":subQ0}),1.0]])]});}
            var Q42;
            {var subQ0=sQuery(id+"F2.wireOp",EDGE,"E156");Q42=makeQuery(id+"F2.imprint","IMPRINT",FACE,{"disambiguationData":[TD([[makeQuery(id+"F2.imprint","IMPRINT",EDGE,{"derivedFrom":subQ0}),1.0]])]});}
            var Q43;
            {var subQ0=sQuery(id+"F2.wireOp",EDGE,"E160");Q43=makeQuery(id+"F2.imprint","IMPRINT",FACE,{"disambiguationData":[TD([[makeQuery(id+"F2.imprint","IMPRINT",EDGE,{"derivedFrom":subQ0}),1.0]])]});}
            var Q44;
            {var subQ0=sQuery(id+"F2.wireOp",EDGE,"E164");Q44=makeQuery(id+"F2.imprint","IMPRINT",FACE,{"disambiguationData":[TD([[makeQuery(id+"F2.imprint","IMPRINT",EDGE,{"derivedFrom":subQ0}),1.0]])]});}
            var Q45;
            {var subQ0=sQuery(id+"F2.wireOp",EDGE,"E168");Q45=makeQuery(id+"F2.imprint","IMPRINT",FACE,{"disambiguationData":[TD([[makeQuery(id+"F2.imprint","IMPRINT",EDGE,{"derivedFrom":subQ0}),1.0]])]});}
            var Q46;
            {var subQ0=sQuery(id+"F2.wireOp",EDGE,"E172");Q46=makeQuery(id+"F2.imprint","IMPRINT",FACE,{"disambiguationData":[TD([[makeQuery(id+"F2.imprint","IMPRINT",EDGE,{"derivedFrom":subQ0}),1.0]])]});}
            var Q47;
            {var subQ0=sQuery(id+"F2.wireOp",EDGE,"E176");Q47=makeQuery(id+"F2.imprint","IMPRINT",FACE,{"disambiguationData":[TD([[makeQuery(id+"F2.imprint","IMPRINT",EDGE,{"derivedFrom":subQ0}),1.0]])]});}
            var Q48;
            {var subQ0=sQuery(id+"F2.wireOp",EDGE,"E180");Q48=makeQuery(id+"F2.imprint","IMPRINT",FACE,{"disambiguationData":[TD([[makeQuery(id+"F2.imprint","IMPRINT",EDGE,{"derivedFrom":subQ0}),1.0]])]});}
            var Q49;
            {var subQ0=sQuery(id+"F2.wireOp",EDGE,"E184");Q49=makeQuery(id+"F2.imprint","IMPRINT",FACE,{"disambiguationData":[TD([[makeQuery(id+"F2.imprint","IMPRINT",EDGE,{"derivedFrom":subQ0}),1.0]])]});}
            extrude(context, id + "F3", {"entities" : qUnion([Q0, Q1, Q2, Q3, Q4, Q5, Q6, Q7, Q8, Q9, Q10, Q11, Q12, Q13, Q14, Q15, Q16, Q17, Q18, Q19, Q20, Q21, Q22, Q23, Q24, Q25, Q26, Q27, Q28, Q29, Q30, Q31, Q32, Q33, Q34, Q35, Q36, Q37, Q38, Q39, Q40, Q41, Q42, Q43, Q44, Q45, Q46, Q47, Q48, Q49]), "operationType" : NewBodyOperationType.REMOVE, "oppositeDirection" : true, "depth" : 25.4 * mm});
        }
    });
